# Revit family: DC_Rheem_PLM_CPE11_BackToBack
name_source: partatom
category: Plumbing Fixtures
revit_build: Autodesk Revit 2018 (Build: 20170223_1515(x64)
units: mm (PartAtom-declared; Revit-internal decimal feet)

## family parameters
Cut with Voids When Loaded = No
Host = Face
Part Type = Normal
Room Calculation Point = No
Round Connector Dimension = Use Radius
Shared = No

## types (2) — shared parameters
Cold Water Pipe Diameter = 50 mm  [stored 0.164042 ft]
ColdWaterPipeRadius_ANZRS = 25 mm  [stored 0.082021 ft]
GasPipeDiameterD3_ANZRS = 50 mm  [stored 0.164042 ft]
GasPipeRadius_ANZRS = 25 mm  [stored 0.082021 ft]
HotWaterOutletDiameterD2_ANZRS = 50 mm  [stored 0.164042 ft]
HotWaterOutletRadius_ANZRS = 25 mm  [stored 0.082021 ft]
HotWaterReturnDiameterD1_ANZRS = 25 mm  [stored 0.082021 ft]
HotWaterReturnRadius_ANZRS = 12.5 mm  [stored 0.0410105 ft]
Length_ANZRS = 2160 mm
Manufacturer = Rheem
Materials_ANZRS = Rheem - Antique White
Type Comments = 145L/min @ 50°C rise  -Dual 50% capacity pump and controller included - Room sealed coaxial flue components available from Rheem.
URL = http://www.rheem.com.au
zero-valued in all types: Default Elevation

## per-type parameters (varying)
| type | Model |
| Commpak - Gas Continuous Flow - Outdoor - 2255 MJ/h Natural gas free standing frame - back to back | CPE11NB |
| Commpak - Gas Continuous Flow - Outdoor - 2255 MJ/h Propane gas free standing frame - back to back | CPE111PB |

note: column(s) folded — value = type name in every type: Description

note: [stored X ft] marks values corroborated as IEEE doubles in the binary element streams (Revit-internal decimal feet)

## geometry (parser evidence)
native form markers: Sweep x33
no freeform markers — native parametric forms only
